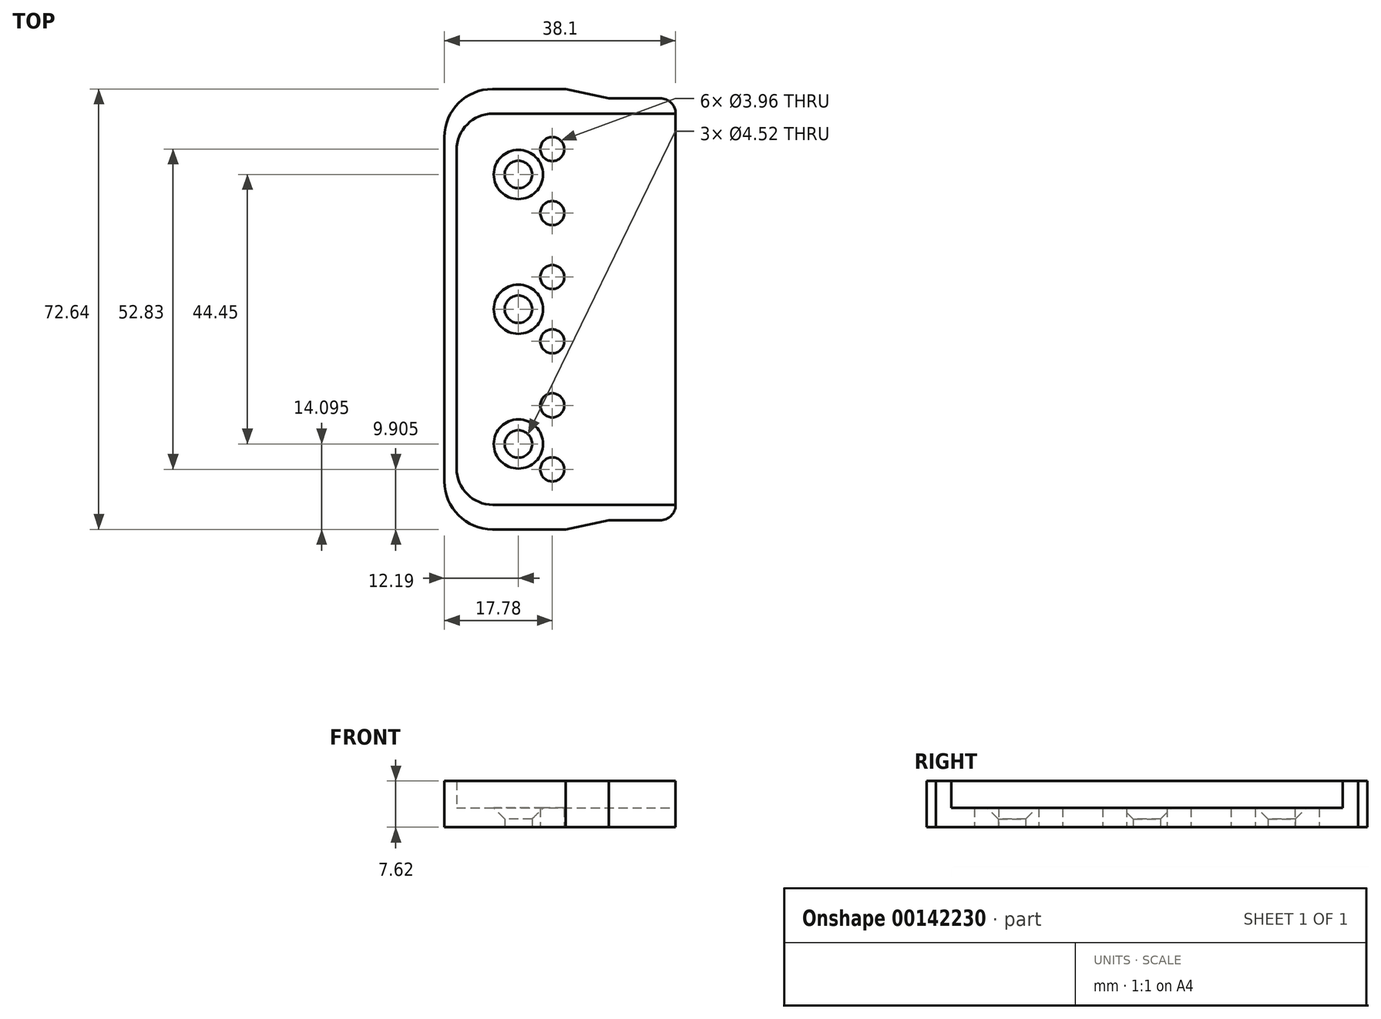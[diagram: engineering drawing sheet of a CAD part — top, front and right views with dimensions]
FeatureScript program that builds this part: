
annotation { "Feature Type Name" : "Feature", "Feature Type Description" : "" }
export const myFeature = defineFeature(function(context is Context, id is Id, definition is map)
    precondition{}
    {
        {
            var Q0;
            Q0=qCreatedBy(makeId("Top.planeOp"),FACE);
            var sketch = newSketch(context, id + "F0", { "sketchPlane" : qUnion([Q0])});
            skLineSegment(sketch, "E0", {"start": v(0, 0) * mm, "end": v(0, 32.25) * mm});
            skLineSegment(sketch, "E1", {"start": v(69.67, 0) * mm, "end": v(-138.57, 0) * mm, "construction": true});
            skLineSegment(sketch, "E2", {"start": v(-38.1, 0) * mm, "end": v(-38.1, 28.4) * mm});
            skLineSegment(sketch, "E3", {"start": v(-30.18, 36.32) * mm, "end": v(-18.1, 36.32) * mm});
            skLineSegment(sketch, "E4", {"start": v(-18.1, 36.32) * mm, "end": v(-11, 34.8) * mm});
            skLineSegment(sketch, "E5", {"start": v(-11, 34.8) * mm, "end": v(-2.54, 34.8) * mm});
            skLineSegment(sketch, "E6", {"start": v(-20.32, 48.76) * mm, "end": v(-20.32, -63.6) * mm, "construction": true});
            skCircle(sketch, "E7", {"center": v(-20.32, 26.41) * mm, "radius": 1.98 * mm});
            skCircle(sketch, "E8", {"center": v(-20.32, 15.85) * mm, "radius": 1.98 * mm});
            skCircle(sketch, "E9", {"center": v(-20.32, 5.3) * mm, "radius": 1.98 * mm});
            skCircle(sketch, "E10.MirrorC", {"center": v(-20.32, -15.85) * mm, "radius": 1.98 * mm});
            skLineSegment(sketch, "E11.MirrorCS", {"start": v(-11, -34.8) * mm, "end": v(-2.54, -34.8) * mm});
            skLineSegment(sketch, "E12.MirrorCS", {"start": v(-18.1, -36.32) * mm, "end": v(-11, -34.8) * mm});
            skLineSegment(sketch, "E13.MirrorCS", {"start": v(-38.1, 0) * mm, "end": v(-38.1, -28.4) * mm});
            skLineSegment(sketch, "E14.MirrorCS", {"start": v(-20.32, -48.76) * mm, "end": v(-20.32, 63.6) * mm, "construction": true});
            skLineSegment(sketch, "E15.MirrorCS", {"start": v(0, 0) * mm, "end": v(0, -32.26) * mm});
            skLineSegment(sketch, "E16.MirrorCS", {"start": v(-30.18, -36.32) * mm, "end": v(-18.1, -36.32) * mm});
            skCircle(sketch, "E17.MirrorC", {"center": v(-20.32, -26.41) * mm, "radius": 1.98 * mm});
            skCircle(sketch, "E18.MirrorC", {"center": v(-20.32, -5.3) * mm, "radius": 1.98 * mm});
            skPoint(sketch, "E19.visualSharp", {"position": v(-38.1, 36.32) * mm});
            skArc(sketch, "E19.filletArc", {"start": v(-30.18, 36.32) * mm, "mid": v(-35.78, 34) * mm, "end": v(-38.1, 28.4) * mm});
            skPoint(sketch, "E20.visualSharp", {"position": v(-38.1, -36.32) * mm});
            skArc(sketch, "E20.filletArc", {"start": v(-38.1, -28.4) * mm, "mid": v(-35.78, -34) * mm, "end": v(-30.18, -36.32) * mm});
            skPoint(sketch, "E21.visualSharp", {"position": v(0, 34.8) * mm});
            skArc(sketch, "E21.filletArc", {"start": v(0, 32.25) * mm, "mid": v(-0.74, 34.05) * mm, "end": v(-2.54, 34.8) * mm});
            skPoint(sketch, "E22.visualSharp", {"position": v(0, -34.8) * mm});
            skArc(sketch, "E22.filletArc", {"start": v(-2.54, -34.8) * mm, "mid": v(-0.74, -34.05) * mm, "end": v(0, -32.26) * mm});
            skLineSegment(sketch, "E23", {"start": v(-25.91, 54.64) * mm, "end": v(-25.91, -67.06) * mm, "construction": true});
            skCircle(sketch, "E24", {"center": v(-25.91, -22.23) * mm, "radius": 2.26 * mm});
            skCircle(sketch, "E25.MirrorC", {"center": v(-25.91, 22.23) * mm, "radius": 2.26 * mm});
            skCircle(sketch, "E26", {"center": v(-25.91, 0) * mm, "radius": 2.26 * mm});
            skLineSegment(sketch, "E27", {"start": v(0, -32.26) * mm, "end": v(-30.1, -32.26) * mm});
            skLineSegment(sketch, "E28", {"start": v(-36.1, -26.26) * mm, "end": v(-36.1, 26.25) * mm});
            skLineSegment(sketch, "E29", {"start": v(-30.1, 32.25) * mm, "end": v(0, 32.25) * mm});
            skPoint(sketch, "E30.visualSharp", {"position": v(-36.1, 32.25) * mm});
            skArc(sketch, "E30.filletArc", {"start": v(-30.1, 32.25) * mm, "mid": v(-34.34, 30.5) * mm, "end": v(-36.1, 26.25) * mm});
            skPoint(sketch, "E31.visualSharp", {"position": v(-36.1, -32.26) * mm});
            skArc(sketch, "E31.filletArc", {"start": v(-36.1, -26.26) * mm, "mid": v(-34.34, -30.5) * mm, "end": v(-30.1, -32.26) * mm});
            skSolve(sketch);
        }
        {
            var Q0;
            Q0 = qSketchRegion(id + "F0", true);
            extrude(context, id + "F1", {"entities" : qUnion([Q0]), "depth" : 3.17 * mm});
        }
        {
            var Q0;
            Q0=makeQuery(id+"F0.imprint","IMPRINT",FACE,{"disambiguationData":[TD([[makeQuery(id+"F0.imprint","IMPRINT",EDGE,{"derivedFrom":sQuery(id+"F0.wireOp",EDGE,"E2")}),-1.0]])]});
            extrude(context, id + "F2", {"entities" : qUnion([Q0]), "operationType" : NewBodyOperationType.ADD, "depth" : (2.54 * 3) * mm});
        }
        {
            var Q0;
            Q0=makeQuery(id+"F1.opExtrude","CAP_EDGE",EDGE,{"disambiguationData":[OSD([sQuery(id+"F0.wireOp",EDGE,"E24")])],"isStart":false});
            var Q1;
            Q1=makeQuery(id+"F1.opExtrude","CAP_EDGE",EDGE,{"disambiguationData":[OSD([sQuery(id+"F0.wireOp",EDGE,"E26")])],"isStart":false});
            var Q2;
            Q2=makeQuery(id+"F1.opExtrude","CAP_EDGE",EDGE,{"disambiguationData":[OSD([sQuery(id+"F0.wireOp",EDGE,"E25.MirrorC")])],"isStart":false});
            chamfer(context, id + "F3", {"entities" : qUnion([Q0, Q1, Q2]), "width" : 1.8 * mm, "tangentPropagation" : true});
        }
    });
